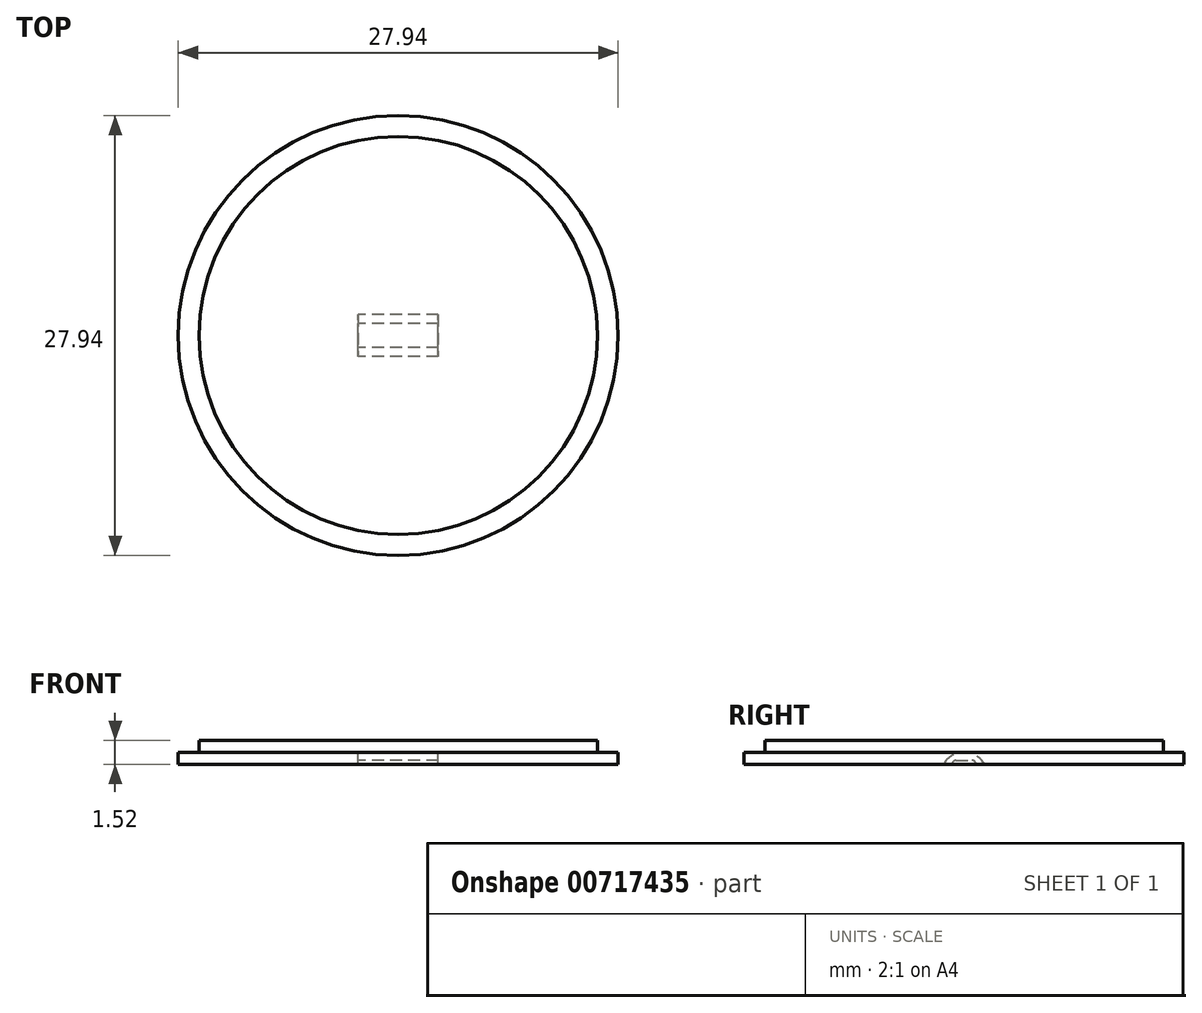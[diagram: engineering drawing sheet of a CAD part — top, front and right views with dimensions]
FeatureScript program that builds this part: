
annotation { "Feature Type Name" : "Feature", "Feature Type Description" : "" }
export const myFeature = defineFeature(function(context is Context, id is Id, definition is map)
    precondition{}
    {
        {
            var Q0;
            Q0=qCreatedBy(makeId("Top.planeOp"),FACE);
            var sketch = newSketch(context, id + "F0", { "sketchPlane" : qUnion([Q0])});
            skCircle(sketch, "E0", {"center": v(0, 0) * mm, "radius": 12.65 * mm});
            skSolve(sketch);
        }
        {
            var Q0;
            Q0 = qSketchRegion(id + "F0", true);
            extrude(context, id + "F1", {"entities" : qUnion([Q0]), "depth" : 1.52 * mm, "offsetDistance" : 25.4 * mm});
        }
        {
            var Q0;
            Q0=qCreatedBy(makeId("Top.planeOp"),FACE);
            var sketch = newSketch(context, id + "F2", { "sketchPlane" : qUnion([Q0])});
            skCircle(sketch, "E1", {"center": v(0, 0) * mm, "radius": 13.97 * mm});
            skSolve(sketch);
        }
        {
            var Q0;
            Q0 = qSketchRegion(id + "F2", true);
            extrude(context, id + "F3", {"entities" : qUnion([Q0]), "operationType" : NewBodyOperationType.ADD, "depth" : 0.76 * mm, "offsetDistance" : 25.4 * mm});
        }
        {
            var Q0;
            Q0=qCreatedBy(makeId("Front.planeOp"),FACE);
            var sketch = newSketch(context, id + "F4", { "sketchPlane" : qUnion([Q0])});
            skLineSegment(sketch, "E2.bottom", {"start": v(2.54, -0.76) * mm, "end": v(-2.54, -0.76) * mm});
            skLineSegment(sketch, "E2.top", {"start": v(2.54, 0.76) * mm, "end": v(-2.54, 0.76) * mm});
            skLineSegment(sketch, "E2.left", {"start": v(2.54, -0.76) * mm, "end": v(2.54, 0.76) * mm});
            skLineSegment(sketch, "E2.right", {"start": v(-2.54, -0.76) * mm, "end": v(-2.54, 0.76) * mm});
            skPoint(sketch, "E2.middle", {"position": v(0, 0) * mm});
            skSolve(sketch);
        }
        {
            var Q0;
            Q0 = qSketchRegion(id + "F4", true);
            var Q1;
            Q1=sQuery(id+"F4.wireOp",EDGE,"E2.bottom");
            revolve(context, id + "F5", {"operationType" : NewBodyOperationType.REMOVE, "surfaceOperationType" : NewSurfaceOperationType.NEW, "entities" : qUnion([Q0]), "axis" : qUnion([Q1]), "revolveType" : RevolveType.FULL, "oppositeDirection" : true});
        }
        {
            var Q0;
            Q0=qCreatedBy(makeId("Top.planeOp"),FACE);
            var sketch = newSketch(context, id + "F6", { "sketchPlane" : qUnion([Q0])});
            skLineSegment(sketch, "E3.bottom", {"start": v(2.54, -0.76) * mm, "end": v(-2.54, -0.76) * mm});
            skLineSegment(sketch, "E3.top", {"start": v(2.54, 0.76) * mm, "end": v(-2.54, 0.76) * mm});
            skLineSegment(sketch, "E3.left", {"start": v(2.54, -0.76) * mm, "end": v(2.54, 0.76) * mm});
            skLineSegment(sketch, "E3.right", {"start": v(-2.54, -0.76) * mm, "end": v(-2.54, 0.76) * mm});
            skPoint(sketch, "E3.middle", {"position": v(0, 0) * mm});
            skSolve(sketch);
        }
        {
            var Q0;
            Q0 = qSketchRegion(id + "F6", true);
            extrude(context, id + "F7", {"entities" : qUnion([Q0]), "depth" : 0.25 * mm, "offsetDistance" : 25.4 * mm});
        }
        {
            var Q0;
            Q0=makeQuery(id+"F7.opExtrude","CAP_EDGE",EDGE,{"disambiguationData":[OSD([sQuery(id+"F6.wireOp",EDGE,"E3.top")])],"isStart":false});
            var Q1;
            Q1=makeQuery(id+"F7.opExtrude","CAP_EDGE",EDGE,{"disambiguationData":[OSD([sQuery(id+"F6.wireOp",EDGE,"E3.bottom")])],"isStart":false});
            fillet(context, id + "F8", {"entities" : qUnion([Q0, Q1]), "radius" : 0.25 * mm, "tangentPropagation" : true, "allowEdgeOverflow" : false});
        }
    });
